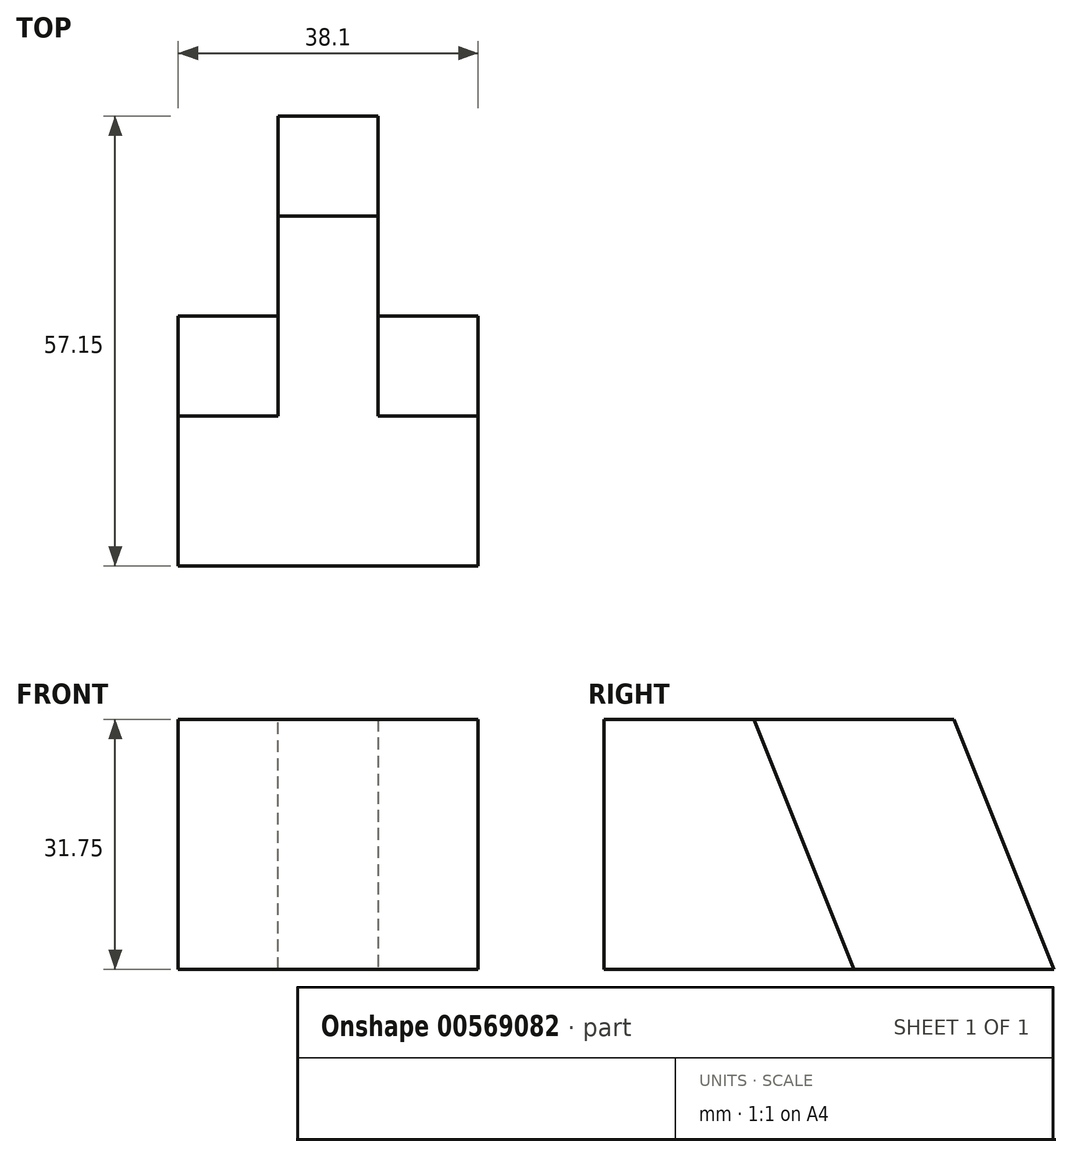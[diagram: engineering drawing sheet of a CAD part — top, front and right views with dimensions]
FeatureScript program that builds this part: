
annotation { "Feature Type Name" : "Feature", "Feature Type Description" : "" }
export const myFeature = defineFeature(function(context is Context, id is Id, definition is map)
    precondition{}
    {
        {
            var Q0;
            Q0=qCreatedBy(makeId("Top.planeOp"),FACE);
            var sketch = newSketch(context, id + "F0", { "sketchPlane" : qUnion([Q0])});
            skLineSegment(sketch, "E0", {"start": v(0, 0) * mm, "end": v(0, 57.15) * mm});
            skLineSegment(sketch, "E1", {"start": v(0, 57.15) * mm, "end": v(38.1, 57.15) * mm});
            skLineSegment(sketch, "E2", {"start": v(38.1, 57.15) * mm, "end": v(38.1, 0) * mm});
            skLineSegment(sketch, "E3", {"start": v(38.1, 0) * mm, "end": v(0, 0) * mm});
            skSolve(sketch);
        }
        {
            var Q0;
            Q0=makeQuery(id+"F0.imprint","IMPRINT",FACE,{"disambiguationData":[TD([[makeQuery(id+"F0.imprint","IMPRINT",EDGE,{"derivedFrom":sQuery(id+"F0.wireOp",EDGE,"E0")}),-1.0]])]});
            extrude(context, id + "F1", {"entities" : qUnion([Q0]), "depth" : 31.75 * mm, "offsetDistance" : 25.4 * mm});
        }
        {
            var Q0;
            Q0=makeQuery(id+"F1.opExtrude","SWEPT_FACE",FACE,{"disambiguationData":[OSD([sQuery(id+"F0.wireOp",EDGE,"E3")])]});
            var sketch = newSketch(context, id + "F2", { "sketchPlane" : qUnion([Q0])});
            skLineSegment(sketch, "E4", {"start": v(25.4, 31.75) * mm, "end": v(25.4, 0) * mm});
            skSolve(sketch);
        }
        {
            var Q0;
            Q0 = qSketchRegion(id + "F2", true);
            var Q1;
            {var subQ0=sQuery(id+"F2.wireOp",EDGE,"E4");Q1=makeQuery(id+"F2.imprint","IMPRINT",FACE,{"disambiguationData":[TD([[makeQuery(id+"F2.imprint","IMPRINT",EDGE,{"derivedFrom":subQ0}),-1.0]])]});}
            extrude(context, id + "F3", {"entities" : qUnion([Q0, Q1]), "operationType" : NewBodyOperationType.REMOVE, "oppositeDirection" : true, "depth" : 76.2 * mm, "offsetDistance" : 25.4 * mm});
        }
        {
            var Q0;
            Q0=makeQuery(id+"F1.opExtrude","SWEPT_FACE",FACE,{"disambiguationData":[OSD([sQuery(id+"F0.wireOp",EDGE,"E2")])]});
            var sketch = newSketch(context, id + "F4", { "sketchPlane" : qUnion([Q0])});
            skLineSegment(sketch, "E5", {"start": v(0, 31.75) * mm, "end": v(19.05, 31.75) * mm});
            skLineSegment(sketch, "E6", {"start": v(0, 0) * mm, "end": v(0, 31.75) * mm});
            skLineSegment(sketch, "E7", {"start": v(19.05, 31.75) * mm, "end": v(31.75, 0) * mm});
            skLineSegment(sketch, "E8", {"start": v(31.75, 0) * mm, "end": v(0, 0) * mm});
            skSolve(sketch);
        }
        {
            var Q0;
            Q0=makeQuery(id+"F4.imprint","IMPRINT",FACE,{"disambiguationData":[TD([[makeQuery(id+"F4.imprint","IMPRINT",EDGE,{"derivedFrom":sQuery(id+"F4.wireOp",EDGE,"E5")}),1.0]])]});
            extrude(context, id + "F5", {"entities" : qUnion([Q0]), "operationType" : NewBodyOperationType.ADD, "depth" : 12.7 * mm, "offsetDistance" : 25.4 * mm});
        }
        {
            var Q0;
            Q0=makeQuery(id+"F3.boolean.opBoolean","COPY",FACE,{"derivedFrom":makeQuery(id+"F3.opExtrude","SWEPT_FACE",FACE,{"disambiguationData":[OSD([sQuery(id+"F2.wireOp",EDGE,"E4")])]})});
            var sketch = newSketch(context, id + "F6", { "sketchPlane" : qUnion([Q0])});
            skLineSegment(sketch, "E9", {"start": v(-19.05, 31.75) * mm, "end": v(-31.75, 0) * mm});
            skLineSegment(sketch, "E10", {"start": v(-31.75, 0) * mm, "end": v(0, 0) * mm});
            skLineSegment(sketch, "E11", {"start": v(0, 0) * mm, "end": v(0, 31.75) * mm});
            skLineSegment(sketch, "E12", {"start": v(0, 31.75) * mm, "end": v(-19.05, 31.75) * mm});
            skSolve(sketch);
        }
        {
            var Q0;
            Q0=makeQuery(id+"F6.imprint","IMPRINT",FACE,{"disambiguationData":[TD([[makeQuery(id+"F6.imprint","IMPRINT",EDGE,{"derivedFrom":sQuery(id+"F6.wireOp",EDGE,"E9")}),1.0]])]});
            extrude(context, id + "F7", {"entities" : qUnion([Q0]), "operationType" : NewBodyOperationType.ADD, "depth" : 12.7 * mm, "offsetDistance" : 25.4 * mm});
        }
        {
            var Q0;
            Q0=makeQuery(id+"F1.opExtrude","SWEPT_FACE",FACE,{"disambiguationData":[OSD([sQuery(id+"F0.wireOp",EDGE,"E2")])]});
            var sketch = newSketch(context, id + "F8", { "sketchPlane" : qUnion([Q0])});
            skLineSegment(sketch, "E13", {"start": v(44.45, 31.75) * mm, "end": v(57.15, 0) * mm});
            skLineSegment(sketch, "E14", {"start": v(57.15, 0) * mm, "end": v(57.15, 31.75) * mm});
            skLineSegment(sketch, "E15", {"start": v(57.15, 31.75) * mm, "end": v(44.45, 31.75) * mm});
            skSolve(sketch);
        }
        {
            var Q0;
            Q0=makeQuery(id+"F8.imprint","IMPRINT",FACE,{"disambiguationData":[TD([[makeQuery(id+"F8.imprint","IMPRINT",EDGE,{"derivedFrom":sQuery(id+"F8.wireOp",EDGE,"E13")}),1.0]])]});
            extrude(context, id + "F9", {"entities" : qUnion([Q0]), "operationType" : NewBodyOperationType.REMOVE, "oppositeDirection" : true, "depth" : 25.4 * mm, "offsetDistance" : 25.4 * mm});
        }
    });
